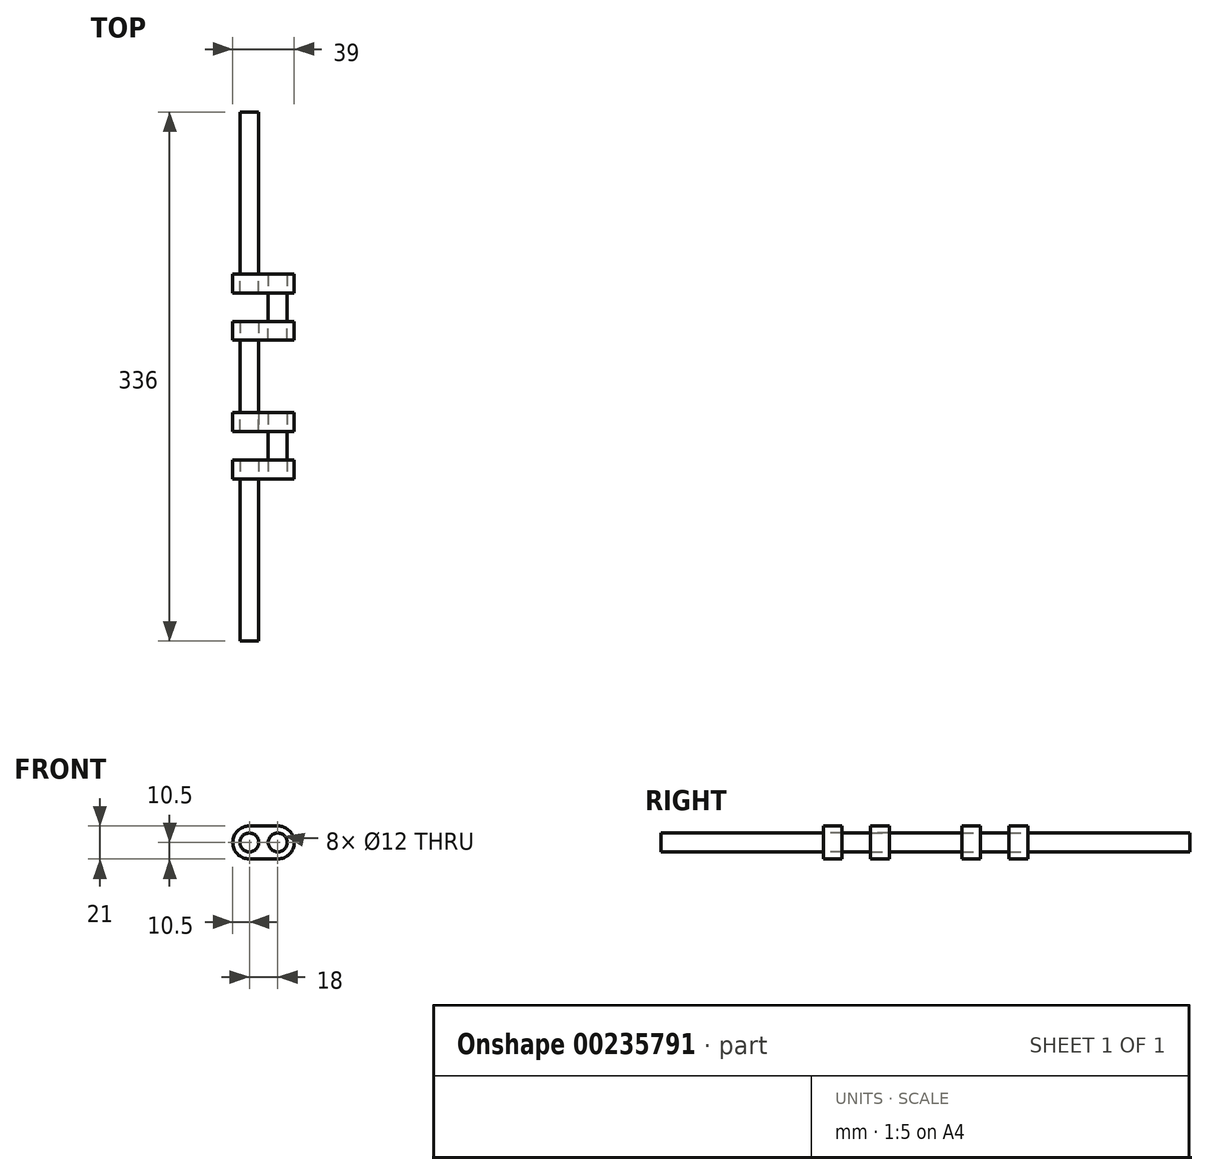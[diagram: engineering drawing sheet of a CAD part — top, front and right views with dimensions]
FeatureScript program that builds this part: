
annotation { "Feature Type Name" : "Feature", "Feature Type Description" : "" }
export const myFeature = defineFeature(function(context is Context, id is Id, definition is map)
    precondition{}
    {
        {
            var Q0;
            Q0=qCreatedBy(makeId("Front.planeOp"),FACE);
            var sketch = newSketch(context, id + "F0", { "sketchPlane" : qUnion([Q0])});
            skCircle(sketch, "E0", {"center": v(0, 0) * mm, "radius": 6 * mm});
            skSolve(sketch);
        }
        {
            var Q0;
            Q0=makeQuery(id+"F0.imprint","IMPRINT",FACE,{"disambiguationData":[TD([[makeQuery(id+"F0.imprint","IMPRINT",EDGE,{"derivedFrom":sQuery(id+"F0.wireOp",EDGE,"E0")}),1.0]])]});
            extrude(context, id + "F1", {"entities" : qUnion([Q0]), "oppositeDirection" : true, "depth" : 103 * mm});
        }
        {
            var Q0;
            Q0=makeQuery(id+"F1.opExtrude","CAP_FACE",FACE,{"disambiguationData":[OSD([sQuery(id+"F0.wireOp",EDGE,"E0")])],"isStart":false});
            var sketch = newSketch(context, id + "F2", { "sketchPlane" : qUnion([Q0])});
            skArc(sketch, "E1", {"start": v(-10.5, 0) * mm, "mid": v(0, -10.5) * mm, "end": v(10.5, 0) * mm});
            skLineSegment(sketch, "E2", {"start": v(-10.5, 0) * mm, "end": v(-10.5, 18) * mm});
            skLineSegment(sketch, "E3.MirrorCS", {"start": v(10.5, 0) * mm, "end": v(10.5, 18) * mm});
            skArc(sketch, "E4.MirrorCS", {"start": v(-10.5, 18) * mm, "mid": v(0, 28.5) * mm, "end": v(10.5, 18) * mm});
            skCircle(sketch, "E5", {"center": v(0, 18) * mm, "radius": 6 * mm});
            skSolve(sketch);
        }
        {
            var Q0;
            Q0=makeQuery(id+"F2.imprint","IMPRINT",FACE,{"disambiguationData":[TD([[makeQuery(id+"F2.imprint","IMPRINT",EDGE,{"derivedFrom":sQuery(id+"F2.wireOp",EDGE,"E1")}),1.0]])]});
            extrude(context, id + "F3", {"entities" : qUnion([Q0]), "depth" : 12 * mm});
        }
        {
            var Q0;
            Q0=makeQuery(id+"F3.opExtrude","CAP_FACE",FACE,{"disambiguationData":[OSD([sQuery(id+"F0.wireOp",EDGE,"E0"),sQuery(id+"F2.wireOp",EDGE,"E1"),sQuery(id+"F2.wireOp",EDGE,"E2"),sQuery(id+"F2.wireOp",EDGE,"E3.MirrorCS"),sQuery(id+"F2.wireOp",EDGE,"E4.MirrorCS"),sQuery(id+"F2.wireOp",EDGE,"E5")])],"isStart":false});
            var sketch = newSketch(context, id + "F4", { "sketchPlane" : qUnion([Q0])});
            skCircle(sketch, "E6", {"center": v(0, 18) * mm, "radius": 6 * mm});
            skSolve(sketch);
        }
        {
            var Q0;
            Q0=makeQuery(id+"F4.imprint","IMPRINT",FACE,{"disambiguationData":[TD([[makeQuery(id+"F4.imprint","IMPRINT",EDGE,{"derivedFrom":sQuery(id+"F4.wireOp",EDGE,"E6")}),1.0]])]});
            extrude(context, id + "F5", {"entities" : qUnion([Q0]), "depth" : 18 * mm});
        }
        {
            var Q0;
            Q0=makeQuery(id+"F5.opExtrude","CAP_FACE",FACE,{"disambiguationData":[OSD([sQuery(id+"F4.wireOp",EDGE,"E6")])],"isStart":false});
            var sketch = newSketch(context, id + "F6", { "sketchPlane" : qUnion([Q0])});
            skArc(sketch, "E7", {"start": v(10.5, 18) * mm, "mid": v(0, 28.5) * mm, "end": v(-10.5, 18) * mm});
            skLineSegment(sketch, "E8", {"start": v(-10.5, 18) * mm, "end": v(-10.5, 0) * mm});
            skLineSegment(sketch, "E9", {"start": v(10.5, 18) * mm, "end": v(10.5, 0) * mm});
            skArc(sketch, "E10", {"start": v(-10.5, 0) * mm, "mid": v(0, -10.5) * mm, "end": v(10.5, 0) * mm});
            skCircle(sketch, "E11", {"center": v(0, 0) * mm, "radius": 6 * mm});
            skSolve(sketch);
        }
        {
            var Q0;
            Q0=makeQuery(id+"F6.imprint","IMPRINT",FACE,{"disambiguationData":[TD([[makeQuery(id+"F6.imprint","IMPRINT",EDGE,{"derivedFrom":sQuery(id+"F6.wireOp",EDGE,"E7")}),1.0]])]});
            extrude(context, id + "F7", {"entities" : qUnion([Q0]), "depth" : 12 * mm});
        }
        {
            var Q0;
            Q0=makeQuery(id+"F7.opExtrude","CAP_FACE",FACE,{"disambiguationData":[OSD([sQuery(id+"F4.wireOp",EDGE,"E6"),sQuery(id+"F6.wireOp",EDGE,"E7"),sQuery(id+"F6.wireOp",EDGE,"E8"),sQuery(id+"F6.wireOp",EDGE,"E9"),sQuery(id+"F6.wireOp",EDGE,"E10"),sQuery(id+"F6.wireOp",EDGE,"E11")])],"isStart":false});
            var sketch = newSketch(context, id + "F8", { "sketchPlane" : qUnion([Q0])});
            skCircle(sketch, "E12", {"center": v(0, 0) * mm, "radius": 6 * mm});
            skSolve(sketch);
        }
        {
            var Q0;
            Q0=makeQuery(id+"F8.imprint","IMPRINT",FACE,{"disambiguationData":[TD([[makeQuery(id+"F8.imprint","IMPRINT",EDGE,{"derivedFrom":sQuery(id+"F8.wireOp",EDGE,"E12")}),1.0]])]});
            extrude(context, id + "F9", {"entities" : qUnion([Q0]), "depth" : 46 * mm});
        }
        {
            var Q0;
            Q0=makeQuery(id+"F9.opExtrude","CAP_FACE",FACE,{"disambiguationData":[OSD([sQuery(id+"F8.wireOp",EDGE,"E12")])],"isStart":false});
            var sketch = newSketch(context, id + "F10", { "sketchPlane" : qUnion([Q0])});
            skArc(sketch, "E13", {"start": v(0, -10.5) * mm, "mid": v(10.5, 0) * mm, "end": v(0, 10.5) * mm});
            skLineSegment(sketch, "E14", {"start": v(0, 10.5) * mm, "end": v(-18, 10.5) * mm});
            skLineSegment(sketch, "E15", {"start": v(0, -10.5) * mm, "end": v(-18, -10.5) * mm});
            skLineSegment(sketch, "E16", {"start": v(-9, -10.5) * mm, "end": v(-9, 10.5) * mm});
            skArc(sketch, "E17.MirrorCS", {"start": v(-18, -10.5) * mm, "mid": v(-28.5, 0) * mm, "end": v(-18, 10.5) * mm});
            skCircle(sketch, "E18", {"center": v(-18, 0) * mm, "radius": 6 * mm});
            skSolve(sketch);
        }
        {
            var Q0;
            {var subQ2=sQuery(id+"F10.wireOp",EDGE,"E13");Q0=makeQuery(id+"F10.imprint","IMPRINT",FACE,{"disambiguationData":[TD([[makeQuery(id+"F10.imprint","IMPRINT",EDGE,{"derivedFrom":subQ2}),1.0]])]});}
            var Q1;
            {var subQ1=sQuery(id+"F10.wireOp",EDGE,"E16");Q1=makeQuery(id+"F10.imprint","IMPRINT",FACE,{"disambiguationData":[TD([[makeQuery(id+"F10.imprint","IMPRINT",EDGE,{"derivedFrom":subQ1}),1.0]])]});}
            extrude(context, id + "F11", {"entities" : qUnion([Q0, Q1]), "depth" : 12 * mm});
        }
        {
            var Q0;
            Q0=makeQuery(id+"F11.opExtrude","CAP_FACE",FACE,{"disambiguationData":[OSD([sQuery(id+"F8.wireOp",EDGE,"E12"),sQuery(id+"F10.wireOp",EDGE,"E13"),sQuery(id+"F10.wireOp",EDGE,"E14"),sQuery(id+"F10.wireOp",EDGE,"E15"),sQuery(id+"F10.wireOp",EDGE,"E17.MirrorCS"),sQuery(id+"F10.wireOp",EDGE,"E18")])],"isStart":false});
            var sketch = newSketch(context, id + "F12", { "sketchPlane" : qUnion([Q0])});
            skCircle(sketch, "E19", {"center": v(-18, 0) * mm, "radius": 6 * mm});
            skSolve(sketch);
        }
        {
            var Q0;
            Q0=makeQuery(id+"F12.imprint","IMPRINT",FACE,{"disambiguationData":[TD([[makeQuery(id+"F12.imprint","IMPRINT",EDGE,{"derivedFrom":sQuery(id+"F12.wireOp",EDGE,"E19")}),1.0]])]});
            extrude(context, id + "F13", {"entities" : qUnion([Q0]), "depth" : 18 * mm});
        }
        {
            var Q0;
            Q0=makeQuery(id+"F13.opExtrude","CAP_FACE",FACE,{"disambiguationData":[OSD([sQuery(id+"F12.wireOp",EDGE,"E19")])],"isStart":false});
            var sketch = newSketch(context, id + "F14", { "sketchPlane" : qUnion([Q0])});
            skArc(sketch, "E20", {"start": v(-18, 10.5) * mm, "mid": v(-28.5, 0) * mm, "end": v(-18, -10.5) * mm});
            skLineSegment(sketch, "E21", {"start": v(-18, -10.5) * mm, "end": v(0, -10.5) * mm});
            skLineSegment(sketch, "E22", {"start": v(-18, 10.5) * mm, "end": v(0, 10.5) * mm});
            skArc(sketch, "E23", {"start": v(0, -10.5) * mm, "mid": v(10.5, 0) * mm, "end": v(0, 10.5) * mm});
            skCircle(sketch, "E24", {"center": v(0, 0) * mm, "radius": 6 * mm});
            skSolve(sketch);
        }
        {
            var Q0;
            Q0=makeQuery(id+"F14.imprint","IMPRINT",FACE,{"disambiguationData":[TD([[makeQuery(id+"F14.imprint","IMPRINT",EDGE,{"derivedFrom":sQuery(id+"F14.wireOp",EDGE,"E20")}),1.0]])]});
            extrude(context, id + "F15", {"entities" : qUnion([Q0]), "depth" : 12 * mm});
        }
        {
            var Q0;
            Q0=makeQuery(id+"F15.opExtrude","CAP_FACE",FACE,{"disambiguationData":[OSD([sQuery(id+"F12.wireOp",EDGE,"E19"),sQuery(id+"F14.wireOp",EDGE,"E20"),sQuery(id+"F14.wireOp",EDGE,"E21"),sQuery(id+"F14.wireOp",EDGE,"E22"),sQuery(id+"F14.wireOp",EDGE,"E23"),sQuery(id+"F14.wireOp",EDGE,"E24")])],"isStart":false});
            var sketch = newSketch(context, id + "F16", { "sketchPlane" : qUnion([Q0])});
            skCircle(sketch, "E25", {"center": v(0, 0) * mm, "radius": 6 * mm});
            skSolve(sketch);
        }
        {
            var Q0;
            Q0=makeQuery(id+"F16.imprint","IMPRINT",FACE,{"disambiguationData":[TD([[makeQuery(id+"F16.imprint","IMPRINT",EDGE,{"derivedFrom":sQuery(id+"F16.wireOp",EDGE,"E25")}),1.0]])]});
            extrude(context, id + "F17", {"entities" : qUnion([Q0]), "depth" : 103 * mm});
        }
        {
            var Q0;
            Q0=makeQuery(id+"F1.opExtrude","CAP_FACE",FACE,{"disambiguationData":[OSD([sQuery(id+"F0.wireOp",EDGE,"E0")])],"isStart":false});
            extrude(context, id + "F18", {"entities" : qUnion([Q0]), "depth" : 12 * mm});
        }
        {
            var Q0;
            Q0=makeQuery(id+"F5.opExtrude","CAP_FACE",FACE,{"disambiguationData":[OSD([sQuery(id+"F4.wireOp",EDGE,"E6")])],"isStart":true});
            extrude(context, id + "F19", {"entities" : qUnion([Q0]), "depth" : 12 * mm});
        }
        {
            var Q0;
            Q0=makeQuery(id+"F9.opExtrude","CAP_FACE",FACE,{"disambiguationData":[OSD([sQuery(id+"F8.wireOp",EDGE,"E12")])],"isStart":true});
            extrude(context, id + "F20", {"entities" : qUnion([Q0]), "depth" : 12 * mm});
        }
        {
            var Q0;
            Q0=makeQuery(id+"F5.opExtrude","CAP_FACE",FACE,{"disambiguationData":[OSD([sQuery(id+"F4.wireOp",EDGE,"E6")])],"isStart":false});
            extrude(context, id + "F21", {"entities" : qUnion([Q0]), "depth" : 12 * mm});
        }
        {
            var Q0;
            Q0=makeQuery(id+"F9.opExtrude","CAP_FACE",FACE,{"disambiguationData":[OSD([sQuery(id+"F8.wireOp",EDGE,"E12")])],"isStart":false});
            extrude(context, id + "F22", {"entities" : qUnion([Q0]), "depth" : 12 * mm});
        }
        {
            var Q0;
            Q0=makeQuery(id+"F13.opExtrude","CAP_FACE",FACE,{"disambiguationData":[OSD([sQuery(id+"F12.wireOp",EDGE,"E19")])],"isStart":false});
            extrude(context, id + "F23", {"entities" : qUnion([Q0]), "depth" : 12 * mm});
        }
        {
            var Q0;
            Q0=makeQuery(id+"F13.opExtrude","CAP_FACE",FACE,{"disambiguationData":[OSD([sQuery(id+"F12.wireOp",EDGE,"E19")])],"isStart":true});
            extrude(context, id + "F24", {"entities" : qUnion([Q0]), "depth" : 12 * mm});
        }
        {
            var Q0;
            Q0=makeQuery(id+"F17.opExtrude","CAP_FACE",FACE,{"disambiguationData":[OSD([sQuery(id+"F16.wireOp",EDGE,"E25")])],"isStart":true});
            extrude(context, id + "F25", {"entities" : qUnion([Q0]), "depth" : 12 * mm});
        }
        {
            var Q0;
            Q0=makeQuery(id+"F7.opExtrude","SWEPT_BODY",BODY,{"disambiguationData":[OSD([sQuery(id+"F4.wireOp",EDGE,"E6"),sQuery(id+"F6.wireOp",EDGE,"E7"),sQuery(id+"F6.wireOp",EDGE,"E8"),sQuery(id+"F6.wireOp",EDGE,"E9"),sQuery(id+"F6.wireOp",EDGE,"E10"),sQuery(id+"F6.wireOp",EDGE,"E11")])]});
            var Q1;
            Q1=makeQuery(id+"F5.opExtrude","SWEPT_BODY",BODY,{"disambiguationData":[OSD([sQuery(id+"F4.wireOp",EDGE,"E6")])]});
            var Q2;
            Q2=makeQuery(id+"F3.opExtrude","SWEPT_BODY",BODY,{"disambiguationData":[OSD([sQuery(id+"F0.wireOp",EDGE,"E0"),sQuery(id+"F2.wireOp",EDGE,"E1"),sQuery(id+"F2.wireOp",EDGE,"E2"),sQuery(id+"F2.wireOp",EDGE,"E3.MirrorCS"),sQuery(id+"F2.wireOp",EDGE,"E4.MirrorCS"),sQuery(id+"F2.wireOp",EDGE,"E5")])]});
            var Q3;
            Q3=makeQuery(id+"F19.opExtrude","SWEPT_BODY",BODY,{"disambiguationData":[OSD([sQuery(id+"F4.wireOp",EDGE,"E6")])]});
            var Q4;
            Q4=makeQuery(id+"F21.opExtrude","SWEPT_BODY",BODY,{"disambiguationData":[OSD([sQuery(id+"F4.wireOp",EDGE,"E6")])]});
            var Q5;
            Q5=makeQuery(id+"F1.opExtrude","SWEPT_FACE",FACE,{"disambiguationData":[OSD([sQuery(id+"F0.wireOp",EDGE,"E0")])]});
            transform(context, id + "F26", {"entities" : qUnion([Q0, Q1, Q2, Q3, Q4]), "transformType" : TransformType.ROTATION, "transformAxis" : qUnion([Q5]), "angle" : 90 * degree, "oppositeDirection" : true, "makeCopy" : false});
        }
    });
